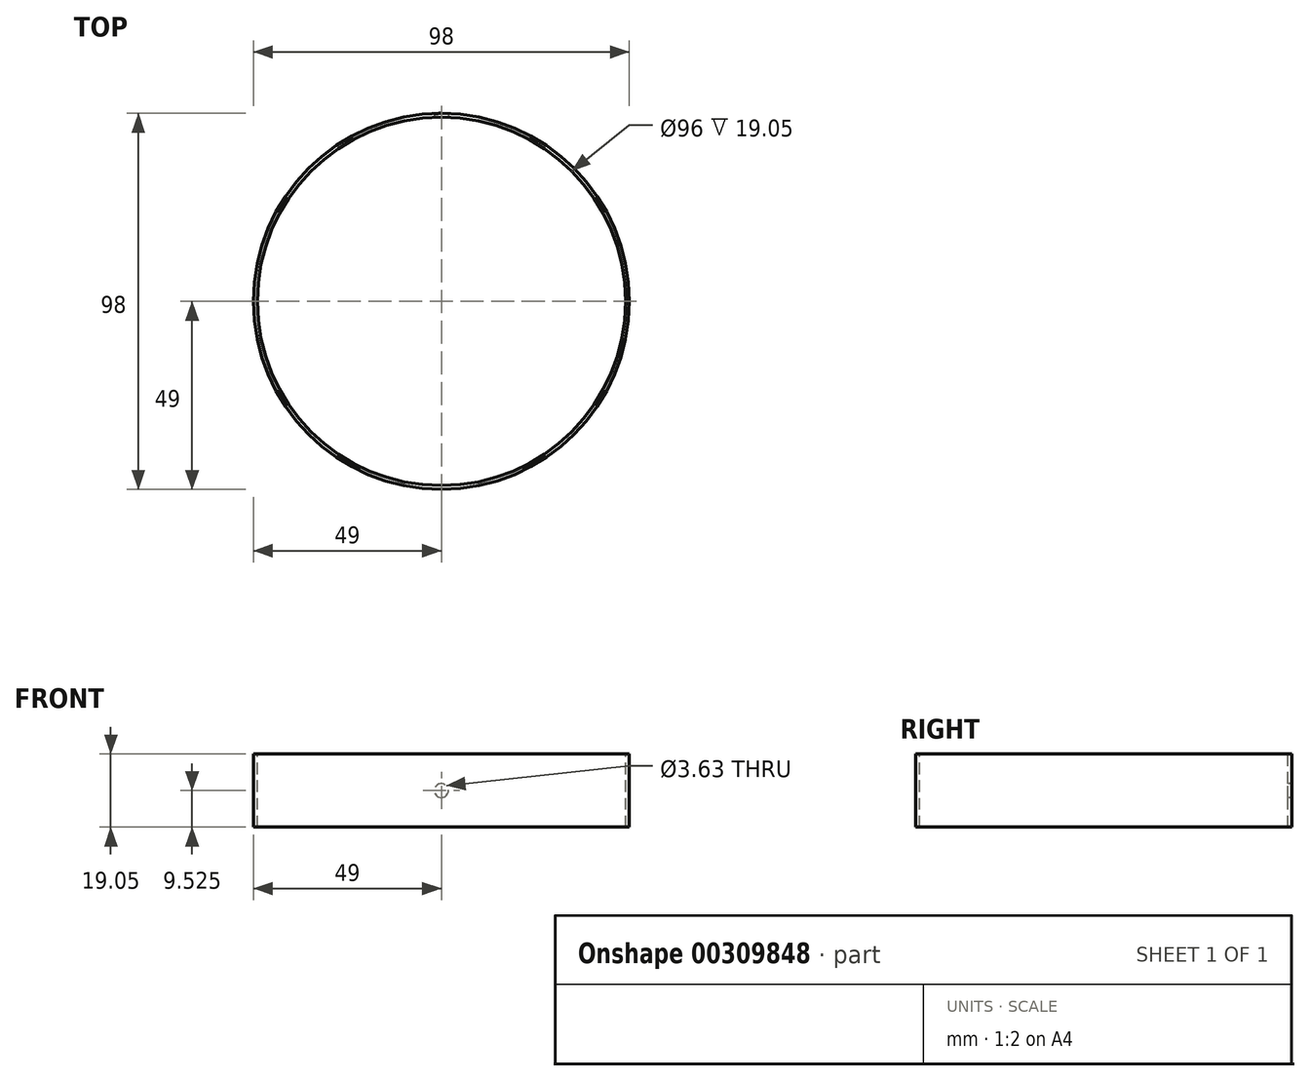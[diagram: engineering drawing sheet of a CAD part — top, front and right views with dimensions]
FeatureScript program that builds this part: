
annotation { "Feature Type Name" : "Feature", "Feature Type Description" : "" }
export const myFeature = defineFeature(function(context is Context, id is Id, definition is map)
    precondition{}
    {
        {
            var Q0;
            Q0=qCreatedBy(makeId("Front.planeOp"),FACE);
            var sketch = newSketch(context, id + "F0", { "sketchPlane" : qUnion([Q0])});
            skLineSegment(sketch, "E0.bottom", {"start": v(0, 0) * mm, "end": v(49, 0) * mm});
            skLineSegment(sketch, "E0.top", {"start": v(0, -19.05) * mm, "end": v(49, -19.05) * mm});
            skLineSegment(sketch, "E0.left", {"start": v(0, 0) * mm, "end": v(0, -19.05) * mm});
            skLineSegment(sketch, "E0.right", {"start": v(49, 0) * mm, "end": v(49, -19.05) * mm});
            skSolve(sketch);
        }
        {
            var Q0;
            Q0=qCreatedBy(makeId("Right.planeOp"),FACE);
            var sketch = newSketch(context, id + "F1", { "sketchPlane" : qUnion([Q0])});
            skLineSegment(sketch, "E1.bottom", {"start": v(0, 0) * mm, "end": v(-48, 0) * mm});
            skLineSegment(sketch, "E1.top", {"start": v(0, -19.05) * mm, "end": v(-48, -19.05) * mm});
            skLineSegment(sketch, "E1.left", {"start": v(0, 0) * mm, "end": v(0, -19.05) * mm});
            skLineSegment(sketch, "E1.right", {"start": v(-48, 0) * mm, "end": v(-48, -19.05) * mm});
            skSolve(sketch);
        }
        {
            var Q0;
            Q0=makeQuery(id+"F0.imprint","IMPRINT",FACE,{"disambiguationData":[TD([[makeQuery(id+"F0.imprint","IMPRINT",EDGE,{"derivedFrom":sQuery(id+"F0.wireOp",EDGE,"E0.bottom")}),-1.0]])]});
            var Q1;
            Q1=sQuery(id+"F1.wireOp",EDGE,"E1.left");
            revolve(context, id + "F2", {"entities" : qUnion([Q0]), "axis" : qUnion([Q1]), "revolveType" : RevolveType.FULL});
        }
        {
            var Q0;
            Q0=makeQuery(id+"F1.imprint","IMPRINT",FACE,{"disambiguationData":[TD([[makeQuery(id+"F1.imprint","IMPRINT",EDGE,{"derivedFrom":sQuery(id+"F1.wireOp",EDGE,"E1.bottom")}),1.0]])]});
            var Q1;
            Q1=sQuery(id+"F1.wireOp",EDGE,"E1.left");
            revolve(context, id + "F3", {"operationType" : NewBodyOperationType.REMOVE, "entities" : qUnion([Q0]), "axis" : qUnion([Q1]), "revolveType" : RevolveType.FULL});
        }
        {
            var Q0;
            Q0=makeQuery(id+"F0.imprint","IMPRINT",FACE,{"disambiguationData":[TD([[makeQuery(id+"F0.imprint","IMPRINT",EDGE,{"derivedFrom":sQuery(id+"F0.wireOp",EDGE,"E0.bottom")}),-1.0]])]});
            var sketch = newSketch(context, id + "F4", { "sketchPlane" : qUnion([Q0])});
            skLineSegment(sketch, "E2", {"start": v(0, 0) * mm, "end": v(0, -9.53) * mm});
            skPoint(sketch, "E3", {"position": v(0, -9.53) * mm});
            skSolve(sketch);
        }
        {
            var Q0;
            Q0=sQuery(id+"F4.wireOp",VERTEX,"E3");
            var Q1;
            Q1=makeQuery(id+"F2.opRevolve","SWEPT_BODY",BODY,{"disambiguationData":[OSD([sQuery(id+"F0.wireOp",EDGE,"E0.bottom"),sQuery(id+"F0.wireOp",EDGE,"E0.top"),sQuery(id+"F0.wireOp",EDGE,"E0.left"),sQuery(id+"F0.wireOp",EDGE,"E0.right")])]});
            hole(context, id + "F5", {"style" : HoleStyle.SIMPLE, "endStyle" : HoleEndStyle.THROUGH, "holeDiameter" : 3.63 * mm, "tappedDepth" : 12.7 * mm, "tapClearance" : 3, "locations" : qUnion([Q0]), "scope" : qUnion([Q1])});
        }
    });
